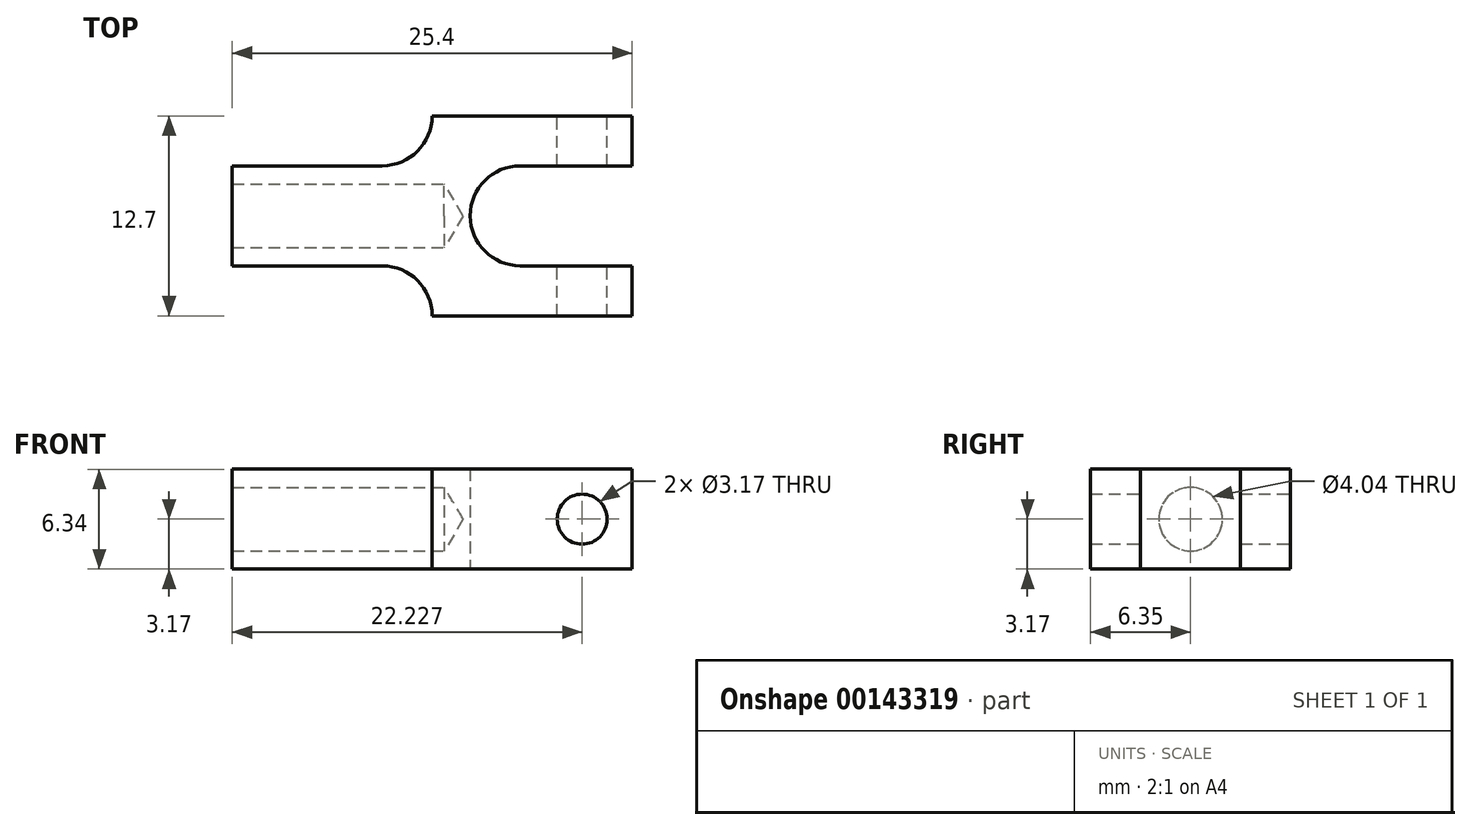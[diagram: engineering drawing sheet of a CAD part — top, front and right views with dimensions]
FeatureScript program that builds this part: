
annotation { "Feature Type Name" : "Feature", "Feature Type Description" : "" }
export const myFeature = defineFeature(function(context is Context, id is Id, definition is map)
    precondition{}
    {
        {
            var Q0;
            Q0=qCreatedBy(makeId("Top.planeOp"),FACE);
            var sketch = newSketch(context, id + "F0", { "sketchPlane" : qUnion([Q0])});
            skLineSegment(sketch, "E0.bottom", {"start": v(-5.59, -6.35) * mm, "end": v(7.11, -6.35) * mm});
            skLineSegment(sketch, "E0.top", {"start": v(-5.59, 6.35) * mm, "end": v(7.11, 6.35) * mm});
            skLineSegment(sketch, "E0.left", {"start": v(-18.29, -3.17) * mm, "end": v(-18.29, 3.17) * mm});
            skLineSegment(sketch, "E0.right", {"start": v(7.11, -6.35) * mm, "end": v(7.11, -3.17) * mm});
            skArc(sketch, "E1", {"start": v(0, 3.18) * mm, "mid": v(-3.18, 0) * mm, "end": v(0, -3.18) * mm});
            skLineSegment(sketch, "E2", {"start": v(0, 3.18) * mm, "end": v(7.11, 3.18) * mm});
            skLineSegment(sketch, "E3", {"start": v(0, -3.18) * mm, "end": v(7.11, -3.17) * mm});
            skLineSegment(sketch, "E4.trimOffspring", {"start": v(7.11, 3.18) * mm, "end": v(7.11, 6.35) * mm});
            skLineSegment(sketch, "E5", {"start": v(-5.59, 6.35) * mm, "end": v(-5.59, 3.18) * mm});
            skLineSegment(sketch, "E6", {"start": v(-5.59, 3.18) * mm, "end": v(-18.29, 3.17) * mm});
            skPoint(sketch, "E7.orphan", {"position": v(-18.29, 6.35) * mm});
            skLineSegment(sketch, "E8.MirrorCS", {"start": v(-5.59, -6.35) * mm, "end": v(-5.59, -3.18) * mm});
            skLineSegment(sketch, "E9.MirrorCS", {"start": v(-5.59, -3.18) * mm, "end": v(-18.29, -3.17) * mm});
            skPoint(sketch, "E10.orphan", {"position": v(-18.29, -6.35) * mm});
            skSolve(sketch);
        }
        {
            var Q0;
            Q0=makeQuery(id+"F0.imprint","IMPRINT",FACE,{"disambiguationData":[TD([[makeQuery(id+"F0.imprint","IMPRINT",EDGE,{"derivedFrom":sQuery(id+"F0.wireOp",EDGE,"E0.bottom")}),1.0]])]});
            extrude(context, id + "F1", {"entities" : qUnion([Q0]), "depth" : 6.35 * mm, "symmetric" : true});
        }
        {
            var Q0;
            Q0=makeQuery(id+"F1.opExtrude","SWEPT_EDGE",EDGE,{"disambiguationData":[OSD([sQuery(id+"F0.wireOp",EDGE,"E8.MirrorCS"),sQuery(id+"F0.wireOp",EDGE,"E9.MirrorCS")])]});
            var Q1;
            Q1=makeQuery(id+"F1.opExtrude","SWEPT_EDGE",EDGE,{"disambiguationData":[OSD([sQuery(id+"F0.wireOp",EDGE,"E5"),sQuery(id+"F0.wireOp",EDGE,"E6")])]});
            fillet(context, id + "F2", {"entities" : qUnion([Q0, Q1]), "radius" : 3.17 * mm, "tangentPropagation" : true, "allowEdgeOverflow" : false});
        }
        {
            var Q0;
            Q0=makeQuery(id+"F1.opExtrude","SWEPT_FACE",FACE,{"disambiguationData":[OSD([sQuery(id+"F0.wireOp",EDGE,"E0.bottom")])]});
            var sketch = newSketch(context, id + "F3", { "sketchPlane" : qUnion([Q0])});
            skCircle(sketch, "E11", {"center": v(3.94, 0) * mm, "radius": 1.39 * mm});
            skSolve(sketch);
        }
        {
            var Q0;
            Q0=sQuery(id+"F3.wireOp",VERTEX,"E11.center");
            var Q1;
            Q1=makeQuery(id+"F1.opExtrude","SWEPT_BODY",BODY,{"disambiguationData":[OSD([sQuery(id+"F0.wireOp",EDGE,"E0.bottom"),sQuery(id+"F0.wireOp",EDGE,"E0.top"),sQuery(id+"F0.wireOp",EDGE,"E0.left"),sQuery(id+"F0.wireOp",EDGE,"E0.right"),sQuery(id+"F0.wireOp",EDGE,"E1"),sQuery(id+"F0.wireOp",EDGE,"E2"),sQuery(id+"F0.wireOp",EDGE,"E3"),sQuery(id+"F0.wireOp",EDGE,"E4.trimOffspring"),sQuery(id+"F0.wireOp",EDGE,"E5"),sQuery(id+"F0.wireOp",EDGE,"E6"),sQuery(id+"F0.wireOp",EDGE,"E8.MirrorCS"),sQuery(id+"F0.wireOp",EDGE,"E9.MirrorCS")])]});
            hole(context, id + "F4", {"style" : HoleStyle.SIMPLE, "endStyle" : HoleEndStyle.THROUGH, "holeDiameter" : 3.17 * mm, "locations" : qUnion([Q0]), "scope" : qUnion([Q1]), "isTappedThrough" : true, "startStyle" : HoleStartStyle.PART});
        }
        {
            var Q0;
            Q0=makeQuery(id+"F1.opExtrude","SWEPT_FACE",FACE,{"disambiguationData":[OSD([sQuery(id+"F0.wireOp",EDGE,"E0.left")])]});
            var sketch = newSketch(context, id + "F5", { "sketchPlane" : qUnion([Q0])});
            skCircle(sketch, "E12", {"center": v(0, 0) * mm, "radius": 1.49 * mm});
            skSolve(sketch);
        }
        {
            var Q0;
            Q0=sQuery(id+"F5.wireOp",VERTEX,"E12.center");
            var Q1;
            Q1=makeQuery(id+"F1.opExtrude","SWEPT_BODY",BODY,{"disambiguationData":[OSD([sQuery(id+"F0.wireOp",EDGE,"E0.bottom"),sQuery(id+"F0.wireOp",EDGE,"E0.top"),sQuery(id+"F0.wireOp",EDGE,"E0.left"),sQuery(id+"F0.wireOp",EDGE,"E0.right"),sQuery(id+"F0.wireOp",EDGE,"E1"),sQuery(id+"F0.wireOp",EDGE,"E2"),sQuery(id+"F0.wireOp",EDGE,"E3"),sQuery(id+"F0.wireOp",EDGE,"E4.trimOffspring"),sQuery(id+"F0.wireOp",EDGE,"E5"),sQuery(id+"F0.wireOp",EDGE,"E6"),sQuery(id+"F0.wireOp",EDGE,"E8.MirrorCS"),sQuery(id+"F0.wireOp",EDGE,"E9.MirrorCS")])]});
            hole(context, id + "F6", {"style" : HoleStyle.SIMPLE, "endStyle" : HoleEndStyle.BLIND, "standardTappedOrClearance" : lookupTablePath({ "standard" : "ANSI", "engagement" : "75%", "pitch" : "32 tpi", "size" : "#10", "type" : "Tapped" }), "standardBlindInLast" : lookupTablePath({ "standard" : "ANSI", "engagement" : "75%", "pitch" : "32 tpi", "size" : "#10", "type" : "Tapped" }), "holeDiameter" : 4.04 * mm, "holeDepth" : 13.46 * mm, "locations" : qUnion([Q0]), "scope" : qUnion([Q1]), "majorDiameter" : 4.83 * mm, "startStyle" : HoleStartStyle.PART});
        }
    });
